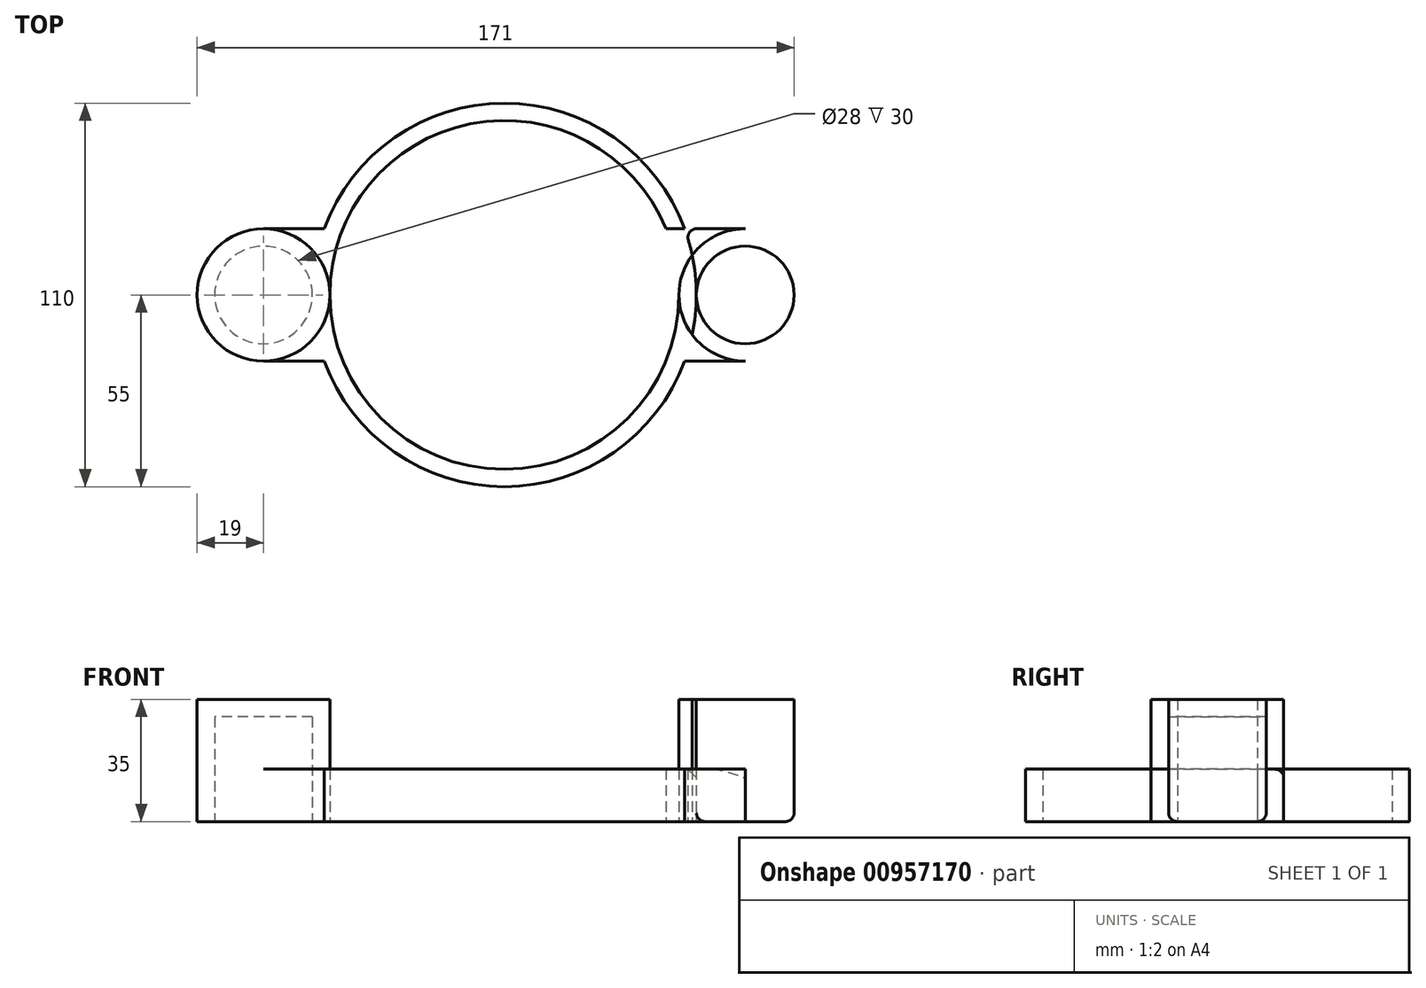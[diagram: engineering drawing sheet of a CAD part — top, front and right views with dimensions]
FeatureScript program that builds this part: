
annotation { "Feature Type Name" : "Feature", "Feature Type Description" : "" }
export const myFeature = defineFeature(function(context is Context, id is Id, definition is map)
    precondition{}
    {
        {
            var Q0;
            Q0=qCreatedBy(makeId("Top.planeOp"),FACE);
            var sketch = newSketch(context, id + "F0", { "sketchPlane" : qUnion([Q0])});
            skCircle(sketch, "E0", {"center": v(0, 0) * mm, "radius": 50 * mm});
            skCircle(sketch, "E1", {"center": v(0, 0) * mm, "radius": 55 * mm});
            skCircle(sketch, "E2", {"center": v(-69, 0) * mm, "radius": 14 * mm});
            skCircle(sketch, "E3", {"center": v(-69, 0) * mm, "radius": 19 * mm});
            skLineSegment(sketch, "E4", {"start": v(-69, 19) * mm, "end": v(-51.61, 19) * mm});
            skLineSegment(sketch, "E5", {"start": v(-69, -19) * mm, "end": v(-51.61, -19) * mm});
            skCircle(sketch, "E6.MirrorC", {"center": v(69, 0) * mm, "radius": 14 * mm});
            skCircle(sketch, "E7.MirrorC", {"center": v(69, 0) * mm, "radius": 19 * mm});
            skLineSegment(sketch, "E8.MirrorCS", {"start": v(69, 19) * mm, "end": v(51.61, 19) * mm});
            skLineSegment(sketch, "E9.MirrorCS", {"start": v(69, -19) * mm, "end": v(51.61, -19) * mm});
            skLineSegment(sketch, "E10", {"start": v(-51.61, -19) * mm, "end": v(51.61, -19) * mm});
            skLineSegment(sketch, "E11", {"start": v(-51.61, 19) * mm, "end": v(51.61, 19) * mm});
            skSolve(sketch);
        }
        {
            var Q0;
            {var subQ4=sQuery(id+"F0.wireOp",EDGE,"E2");Q0=makeQuery(id+"F0.imprint","IMPRINT",FACE,{"disambiguationData":[TD([[makeQuery(id+"F0.imprint","IMPRINT",EDGE,{"derivedFrom":subQ4}),-1.0]])]});}
            var Q1;
            {var subQ0=sQuery(id+"F0.wireOp",EDGE,"E1");var subQ1=makeQuery(id+"F0.imprint","INTERSECT",VERTEX,{"derivedFrom":[subQ0,sQuery(id+"F0.wireOp",EDGE,"E2")]});Q1=makeQuery(id+"F0.imprint","IMPRINT",FACE,{"disambiguationData":[TD([[makeQuery(id+"F0.imprint","IMPRINT",EDGE,{"disambiguationData":[TD([[subQ1,1.0]])],"derivedFrom":subQ0}),1.0]])]});}
            var Q2;
            {var subQ5=sQuery(id+"F0.wireOp",EDGE,"E3");var subQ7=sQuery(id+"F0.wireOp",EDGE,"E0");var subQ8=makeQuery(id+"F0.imprint","INTERSECT",VERTEX,{"derivedFrom":[subQ7,subQ5]});Q2=makeQuery(id+"F0.imprint","IMPRINT",FACE,{"disambiguationData":[TD([[makeQuery(id+"F0.imprint","IMPRINT",EDGE,{"disambiguationData":[TD([[subQ8,1.0]])],"derivedFrom":subQ7}),-1.0]])]});}
            var Q3;
            {var subQ0=sQuery(id+"F0.wireOp",EDGE,"E1");var subQ1=makeQuery(id+"F0.imprint","INTERSECT",VERTEX,{"derivedFrom":[subQ0,sQuery(id+"F0.wireOp",EDGE,"E6.MirrorC")]});Q3=makeQuery(id+"F0.imprint","IMPRINT",FACE,{"disambiguationData":[TD([[makeQuery(id+"F0.imprint","IMPRINT",EDGE,{"disambiguationData":[TD([[subQ1,-1.0]])],"derivedFrom":subQ0}),1.0]])]});}
            var Q4;
            {var subQ0=sQuery(id+"F0.wireOp",EDGE,"E6.MirrorC");Q4=makeQuery(id+"F0.imprint","IMPRINT",FACE,{"disambiguationData":[TD([[makeQuery(id+"F0.imprint","IMPRINT",EDGE,{"derivedFrom":subQ0}),1.0]])]});}
            var Q5;
            {var subQ5=sQuery(id+"F0.wireOp",EDGE,"E3");var subQ7=sQuery(id+"F0.wireOp",EDGE,"E0");var subQ8=makeQuery(id+"F0.imprint","INTERSECT",VERTEX,{"derivedFrom":[subQ7,subQ5]});Q5=makeQuery(id+"F0.imprint","IMPRINT",FACE,{"disambiguationData":[TD([[makeQuery(id+"F0.imprint","IMPRINT",EDGE,{"disambiguationData":[TD([[subQ8,-1.0]])],"derivedFrom":subQ7}),-1.0]])]});}
            var Q6;
            {var subQ0=sQuery(id+"F0.wireOp",EDGE,"E4");Q6=makeQuery(id+"F0.imprint","IMPRINT",FACE,{"disambiguationData":[TD([[makeQuery(id+"F0.imprint","IMPRINT",EDGE,{"derivedFrom":subQ0}),-1.0]])]});}
            var Q7;
            {var subQ0=sQuery(id+"F0.wireOp",EDGE,"E5");Q7=makeQuery(id+"F0.imprint","IMPRINT",FACE,{"disambiguationData":[TD([[makeQuery(id+"F0.imprint","IMPRINT",EDGE,{"derivedFrom":subQ0}),1.0]])]});}
            var Q8;
            {var subQ0=sQuery(id+"F0.wireOp",EDGE,"E8.MirrorCS");Q8=makeQuery(id+"F0.imprint","IMPRINT",FACE,{"disambiguationData":[TD([[makeQuery(id+"F0.imprint","IMPRINT",EDGE,{"derivedFrom":subQ0}),1.0]])]});}
            var Q9;
            {var subQ0=sQuery(id+"F0.wireOp",EDGE,"E9.MirrorCS");Q9=makeQuery(id+"F0.imprint","IMPRINT",FACE,{"disambiguationData":[TD([[makeQuery(id+"F0.imprint","IMPRINT",EDGE,{"derivedFrom":subQ0}),-1.0]])]});}
            var Q10;
            {var subQ0=sQuery(id+"F0.wireOp",EDGE,"E10");var subQ1=sQuery(id+"F0.wireOp",EDGE,"E0");var subQ2=makeQuery(id+"F0.imprint","INTERSECT",VERTEX,{"disambiguationData":[OD(0.0)],"derivedFrom":[subQ1,subQ0]});Q10=makeQuery(id+"F0.imprint","IMPRINT",FACE,{"disambiguationData":[TD([[makeQuery(id+"F0.imprint","IMPRINT",EDGE,{"disambiguationData":[TD([[subQ2,-1.0]])],"derivedFrom":subQ1}),-1.0]])]});}
            var Q11;
            {var subQ0=sQuery(id+"F0.wireOp",EDGE,"E7.MirrorC");var subQ1=sQuery(id+"F0.wireOp",EDGE,"E0");var subQ2=makeQuery(id+"F0.imprint","INTERSECT",VERTEX,{"derivedFrom":[subQ1,subQ0]});Q11=makeQuery(id+"F0.imprint","IMPRINT",FACE,{"disambiguationData":[TD([[makeQuery(id+"F0.imprint","IMPRINT",EDGE,{"disambiguationData":[TD([[subQ2,1.0]])],"derivedFrom":subQ1}),-1.0]])]});}
            var Q12;
            {var subQ0=sQuery(id+"F0.wireOp",EDGE,"E11");var subQ1=sQuery(id+"F0.wireOp",EDGE,"E0");var subQ2=makeQuery(id+"F0.imprint","INTERSECT",VERTEX,{"disambiguationData":[OD(0.0)],"derivedFrom":[subQ1,subQ0]});Q12=makeQuery(id+"F0.imprint","IMPRINT",FACE,{"disambiguationData":[TD([[makeQuery(id+"F0.imprint","IMPRINT",EDGE,{"disambiguationData":[TD([[subQ2,1.0]])],"derivedFrom":subQ1}),-1.0]])]});}
            var Q13;
            {var subQ0=sQuery(id+"F0.wireOp",EDGE,"E11");var subQ1=sQuery(id+"F0.wireOp",EDGE,"E0");var subQ2=makeQuery(id+"F0.imprint","INTERSECT",VERTEX,{"disambiguationData":[OD(0.0)],"derivedFrom":[subQ1,subQ0]});Q13=makeQuery(id+"F0.imprint","IMPRINT",FACE,{"disambiguationData":[TD([[makeQuery(id+"F0.imprint","IMPRINT",EDGE,{"disambiguationData":[TD([[subQ2,-1.0]])],"derivedFrom":subQ1}),-1.0]])]});}
            extrude(context, id + "F1", {"entities" : qUnion([Q0, Q1, Q2, Q3, Q4, Q5, Q6, Q7, Q8, Q9, Q10, Q11, Q12, Q13]), "depth" : 15 * mm, "offsetDistance" : 25 * mm});
        }
        {
            var Q0;
            {var subQ4=sQuery(id+"F0.wireOp",EDGE,"E2");Q0=makeQuery(id+"F0.imprint","IMPRINT",FACE,{"disambiguationData":[TD([[makeQuery(id+"F0.imprint","IMPRINT",EDGE,{"derivedFrom":subQ4}),-1.0]])]});}
            var Q1;
            {var subQ0=sQuery(id+"F0.wireOp",EDGE,"E1");var subQ1=makeQuery(id+"F0.imprint","INTERSECT",VERTEX,{"derivedFrom":[subQ0,sQuery(id+"F0.wireOp",EDGE,"E2")]});Q1=makeQuery(id+"F0.imprint","IMPRINT",FACE,{"disambiguationData":[TD([[makeQuery(id+"F0.imprint","IMPRINT",EDGE,{"disambiguationData":[TD([[subQ1,1.0]])],"derivedFrom":subQ0}),1.0]])]});}
            var Q2;
            {var subQ0=sQuery(id+"F0.wireOp",EDGE,"E6.MirrorC");Q2=makeQuery(id+"F0.imprint","IMPRINT",FACE,{"disambiguationData":[TD([[makeQuery(id+"F0.imprint","IMPRINT",EDGE,{"derivedFrom":subQ0}),1.0]])]});}
            var Q3;
            {var subQ0=sQuery(id+"F0.wireOp",EDGE,"E1");var subQ1=makeQuery(id+"F0.imprint","INTERSECT",VERTEX,{"derivedFrom":[subQ0,sQuery(id+"F0.wireOp",EDGE,"E6.MirrorC")]});Q3=makeQuery(id+"F0.imprint","IMPRINT",FACE,{"disambiguationData":[TD([[makeQuery(id+"F0.imprint","IMPRINT",EDGE,{"disambiguationData":[TD([[subQ1,-1.0]])],"derivedFrom":subQ0}),1.0]])]});}
            extrude(context, id + "F2", {"entities" : qUnion([Q0, Q1, Q2, Q3]), "operationType" : NewBodyOperationType.ADD, "depth" : 35 * mm, "offsetDistance" : 25 * mm});
        }
        {
            var Q0;
            Q0=makeQuery(id+"F2.opExtrude","CAP_FACE",FACE,{"disambiguationData":[OSD([sQuery(id+"F0.wireOp",EDGE,"E2"),sQuery(id+"F0.wireOp",EDGE,"E3")])],"isStart":false});
            var sketch = newSketch(context, id + "F3", { "sketchPlane" : qUnion([Q0])});
            skCircle(sketch, "E12", {"center": v(-69, 0) * mm, "radius": 14 * mm});
            skCircle(sketch, "E13.MirrorC", {"center": v(69, 0) * mm, "radius": 14 * mm});
            skSolve(sketch);
        }
        {
            var Q0;
            Q0=makeQuery(id+"F3.imprint","IMPRINT",FACE,{"disambiguationData":[TD([[makeQuery(id+"F3.imprint","IMPRINT",EDGE,{"derivedFrom":sQuery(id+"F3.wireOp",EDGE,"E12")}),1.0]])]});
            var Q1;
            Q1=makeQuery(id+"F3.imprint","IMPRINT",FACE,{"disambiguationData":[TD([[makeQuery(id+"F3.imprint","IMPRINT",EDGE,{"derivedFrom":sQuery(id+"F3.wireOp",EDGE,"E13.MirrorC")}),-1.0]])]});
            extrude(context, id + "F4", {"entities" : qUnion([Q0, Q1]), "operationType" : NewBodyOperationType.ADD, "oppositeDirection" : true, "depth" : 5 * mm, "offsetDistance" : 25 * mm});
        }
        {
            var Q0;
            {var subQ0=sQuery(id+"F0.wireOp",EDGE,"E11");var subQ1=sQuery(id+"F0.wireOp",EDGE,"E1");Q0=makeQuery(id+"F1.opExtrude","CAP_EDGE",EDGE,{"disambiguationData":[OSD([subQ1]),TDD([makeQuery(id+"F0.imprint","IMPRINT",EDGE,{"disambiguationData":[TD([[makeQuery(id+"F0.imprint","INTERSECT",VERTEX,{"derivedFrom":[subQ1,sQuery(id+"F0.wireOp",EDGE,"E4"),subQ0]}),1.0]])],"derivedFrom":subQ1})])],"isStart":false});}
            var Q1;
            Q1=makeQuery(id+"F2.boolean.opBoolean","SPLIT",EDGE,{"disambiguationData":[OD(0.0)],"derivedFrom":makeQuery(id+"F1.opExtrude","CAP_EDGE",EDGE,{"disambiguationData":[OSD([sQuery(id+"F0.wireOp",EDGE,"E0")])],"isStart":false})});
            var Q2;
            Q2=makeQuery(id+"F1.opExtrude","CAP_EDGE",EDGE,{"disambiguationData":[OSD([sQuery(id+"F0.wireOp",EDGE,"E8.MirrorCS")])],"isStart":false});
            var Q3;
            Q3=makeQuery(id+"F1.opExtrude","CAP_EDGE",EDGE,{"disambiguationData":[OSD([sQuery(id+"F0.wireOp",EDGE,"E4")])],"isStart":false});
            var Q4;
            Q4=makeQuery(id+"F2.opExtrude","CAP_EDGE",EDGE,{"disambiguationData":[OSD([sQuery(id+"F0.wireOp",EDGE,"E3")])],"isStart":false});
            var Q5;
            Q5=makeQuery(id+"F2.opExtrude","CAP_EDGE",EDGE,{"disambiguationData":[OSD([sQuery(id+"F0.wireOp",EDGE,"E7.MirrorC")])],"isStart":false});
            var Q6;
            Q6=makeQuery(id+"F1.opExtrude","SWEPT_EDGE",EDGE,{"disambiguationData":[OSD([sQuery(id+"F0.wireOp",EDGE,"E1"),sQuery(id+"F0.wireOp",EDGE,"E4"),sQuery(id+"F0.wireOp",EDGE,"E11")])]});
            var Q7;
            Q7=makeQuery(id+"F1.opExtrude","SWEPT_EDGE",EDGE,{"disambiguationData":[OSD([sQuery(id+"F0.wireOp",EDGE,"E1"),sQuery(id+"F0.wireOp",EDGE,"E8.MirrorCS"),sQuery(id+"F0.wireOp",EDGE,"E11")])]});
            var Q8;
            Q8=makeQuery(id+"F1.opExtrude","SWEPT_EDGE",EDGE,{"disambiguationData":[OSD([sQuery(id+"F0.wireOp",EDGE,"E1"),sQuery(id+"F0.wireOp",EDGE,"E9.MirrorCS"),sQuery(id+"F0.wireOp",EDGE,"E10")])]});
            var Q9;
            Q9=makeQuery(id+"F1.opExtrude","CAP_EDGE",EDGE,{"disambiguationData":[OSD([sQuery(id+"F0.wireOp",EDGE,"E9.MirrorCS")])],"isStart":false});
            var Q10;
            Q10=makeQuery(id+"F1.opExtrude","CAP_EDGE",EDGE,{"disambiguationData":[OSD([sQuery(id+"F0.wireOp",EDGE,"E5")])],"isStart":false});
            var Q11;
            Q11=makeQuery(id+"F1.opExtrude","SWEPT_EDGE",EDGE,{"disambiguationData":[OSD([sQuery(id+"F0.wireOp",EDGE,"E1"),sQuery(id+"F0.wireOp",EDGE,"E5"),sQuery(id+"F0.wireOp",EDGE,"E10")])]});
            var Q12;
            {var subQ0=sQuery(id+"F0.wireOp",EDGE,"E10");var subQ1=sQuery(id+"F0.wireOp",EDGE,"E1");Q12=makeQuery(id+"F1.opExtrude","CAP_EDGE",EDGE,{"disambiguationData":[OSD([subQ1]),TDD([makeQuery(id+"F0.imprint","IMPRINT",EDGE,{"disambiguationData":[TD([[makeQuery(id+"F0.imprint","INTERSECT",VERTEX,{"derivedFrom":[subQ1,sQuery(id+"F0.wireOp",EDGE,"E5"),subQ0]}),-1.0]])],"derivedFrom":subQ1})])],"isStart":true});}
            var Q13;
            Q13=makeQuery(id+"F1.opExtrude","CAP_EDGE",EDGE,{"disambiguationData":[OSD([sQuery(id+"F0.wireOp",EDGE,"E2")])],"isStart":true});
            var Q14;
            Q14=makeQuery(id+"F1.opExtrude","CAP_EDGE",EDGE,{"disambiguationData":[OSD([sQuery(id+"F0.wireOp",EDGE,"E6.MirrorC")])],"isStart":true});
            fillet(context, id + "F5", {"entities" : qUnion([Q0, Q1, Q2, Q3, Q4, Q5, Q6, Q7, Q8, Q9, Q10, Q11, Q12, Q13, Q14]), "radius" : 2.5 * mm, "tangentPropagation" : true, "allowEdgeOverflow" : false});
        }
    });
